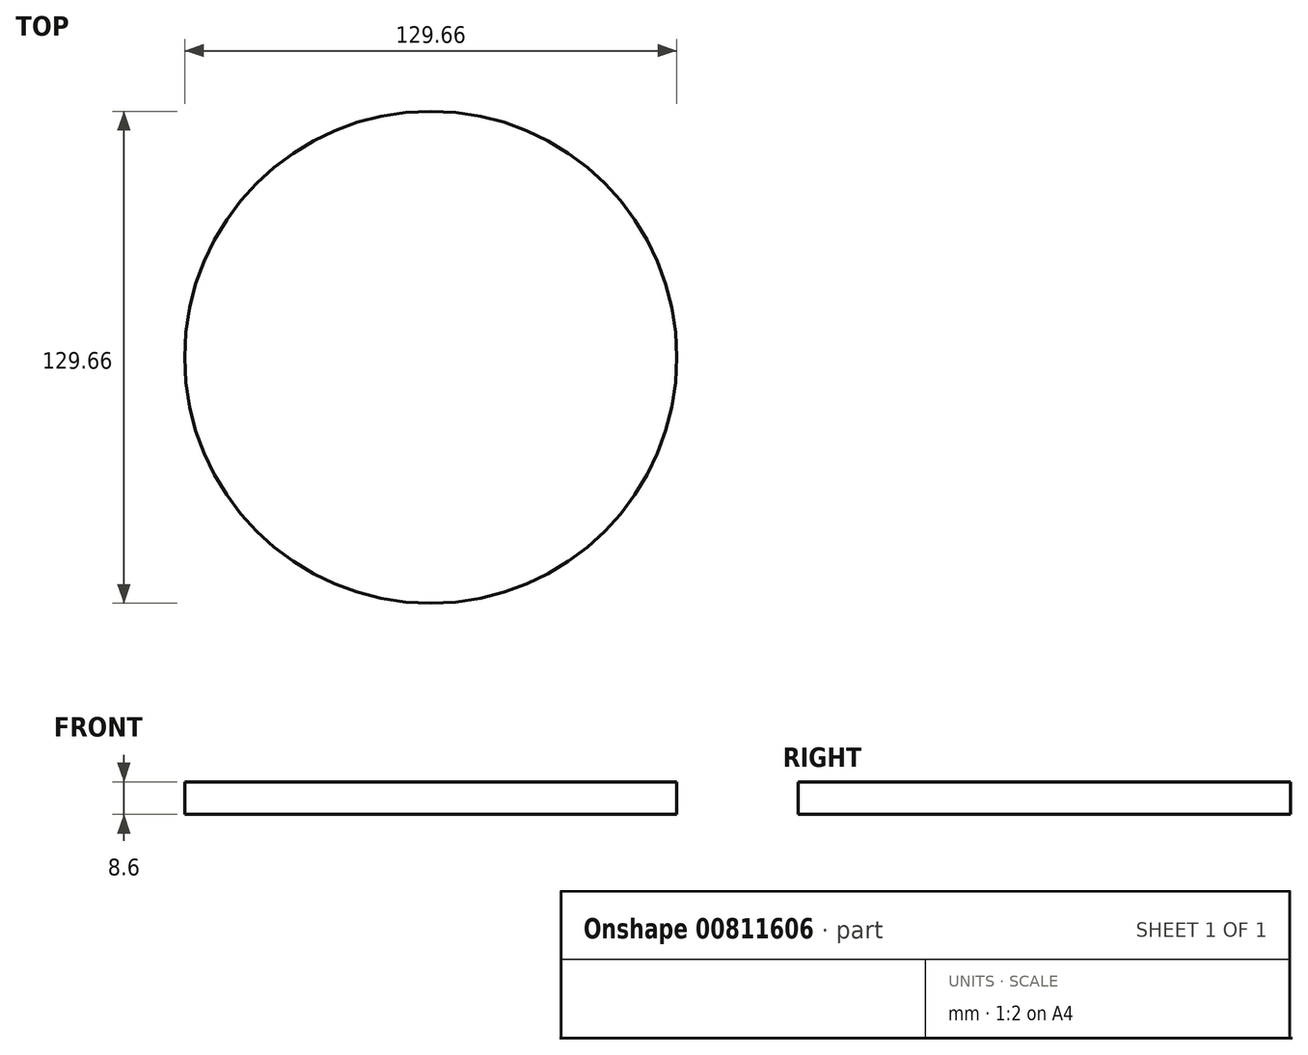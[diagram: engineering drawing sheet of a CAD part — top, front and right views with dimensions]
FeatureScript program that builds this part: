
annotation { "Feature Type Name" : "Feature", "Feature Type Description" : "" }
export const myFeature = defineFeature(function(context is Context, id is Id, definition is map)
    precondition{}
    {
        {
            var Q0;
            Q0=qCreatedBy(makeId("Top.planeOp"),FACE);
            var sketch = newSketch(context, id + "F0", { "sketchPlane" : qUnion([Q0])});
            skCircle(sketch, "E0", {"center": v(0, 0) * mm, "radius": 64.83 * mm});
            skSolve(sketch);
        }
        {
            var Q0;
            Q0 = qSketchRegion(id + "F0", true);
            extrude(context, id + "F1", {"entities" : qUnion([Q0]), "depth" : 8.6 * mm, "offsetDistance" : 25 * mm});
        }
    });
